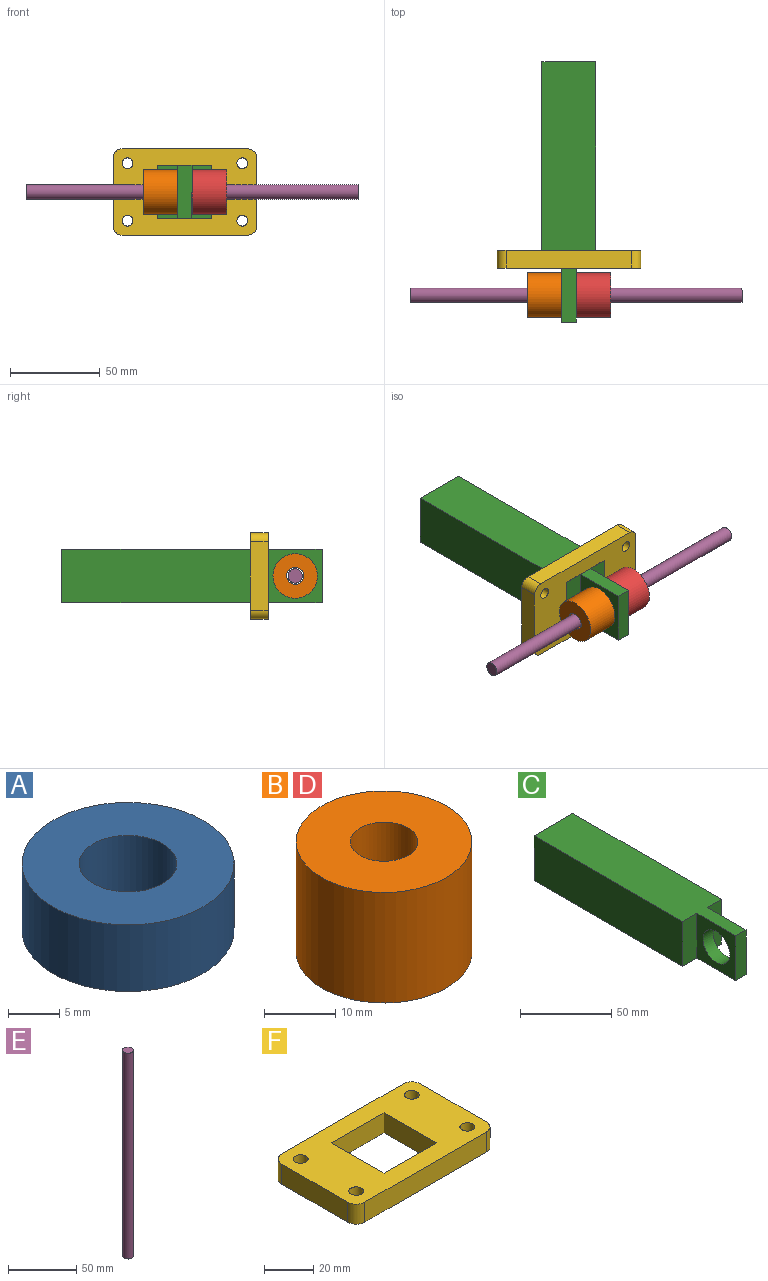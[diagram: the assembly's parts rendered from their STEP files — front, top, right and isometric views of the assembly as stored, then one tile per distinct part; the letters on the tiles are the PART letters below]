
ASSEMBLY  parts=6 mates=5
PART A: 4 faces, bbox 20.6x20.6x7.9 mm
  f0: cylinder r=4.76mm len=9.53mm, axis (0,0,-1), area 237.5mm2, adj f2,f3
  f1: cylinder r=10.32mm len=20.64mm, axis (0,0,-1), area 514.6mm2, adj f2,f3
  f2: plane 20.64x20.64mm, normal (0,0,1), area 263.3mm2, adj f0,f1
  f3: plane 20.64x20.64mm, normal (0,0,-1), area 263.3mm2, adj f0,f1
PART B: 4 faces, bbox 24.8x24.8x19.1 mm
  f0: cylinder r=4.76mm len=19.05mm, axis (0,0,-1), area 570mm2, adj f2,f3
  f1: cylinder r=12.38mm len=24.77mm, axis (0,0,-1), area 1482.1mm2, adj f2,f3
  f2: plane 24.77x24.77mm, normal (0,0,1), area 410.4mm2, adj f0,f1
  f3: plane 24.77x24.77mm, normal (0,0,-1), area 410.4mm2, adj f0,f1
PART C: 11 faces, bbox 30x145x30 mm
  f0: plane 145x30mm, normal (0,0,-1), area 3688.1mm2, adj f3,f4,f5,f6,f7,f8,f9,f10
  f1: plane 145x30mm, normal (0,0,1), area 3688.1mm2, adj f3,f4,f5,f6,f7,f8,f9,f10
  f2: cylinder r=10.32mm len=20.64mm, axis (-1,0,0), area 514.6mm2, adj f4,f5
  f3: plane 30x7.94mm, normal (0,-1,0), area 238.1mm2, adj f0,f1,f4,f5
  f4: plane 30x30mm, normal (1,0,0), area 565.5mm2, adj f0,f1,f2,f3,f6
  f5: plane 30x30mm, normal (-1,0,0), area 565.5mm2, adj f0,f1,f2,f3,f7
  f6: plane 30x11.03mm, normal (0,-1,0), area 330.9mm2, adj f0,f1,f4,f9
  f7: plane 30x11.03mm, normal (0,-1,0), area 330.9mm2, adj f0,f1,f5,f10
  f8: plane 30x30mm, normal (0,1,0), area 900mm2, adj f0,f1,f9,f10
  f9: plane 115x30mm, normal (1,0,0), area 3450mm2, adj f0,f1,f6,f8
  f10: plane 115x30mm, normal (-1,0,0), area 3450mm2, adj f0,f1,f7,f8
PART D: same geometry as B
PART E: 3 faces, bbox 8x8x185 mm
  f0: cylinder r=4mm len=185mm, axis (0,0,-1), area 4649.6mm2, adj f1,f2
  f1: plane 8x8mm, normal (0,0,1), area 50.3mm2, adj f0
  f2: plane 8x8mm, normal (0,0,-1), area 50.3mm2, adj f0
PART F: 18 faces, bbox 80x48x10 mm
  f0: plane 30x10mm, normal (0,-1,0), area 300mm2, adj f1,f7,f8,f9
  f1: plane 30x10mm, normal (-1,0,0), area 300mm2, adj f0,f2,f8,f9
  f2: plane 30x10mm, normal (0,1,0), area 300mm2, adj f1,f7,f8,f9
  f3: plane 70x10mm, normal (0,-1,0), area 700mm2, adj f8,f9,f11,f12
  f4: plane 38x10mm, normal (1,0,0), area 380mm2, adj f8,f9,f12,f13
  f5: plane 70x10mm, normal (0,1,0), area 700mm2, adj f8,f9,f10,f13
  f6: plane 38x10mm, normal (-1,0,0), area 380mm2, adj f8,f9,f10,f11
  f7: plane 30x10mm, normal (1,0,0), area 300mm2, adj f0,f2,f8,f9
  f8: plane 80x48mm, normal (0,0,1), area 2805.4mm2, adj f0,f1,f2,f3,f4,f5,f6,f7
  f9: plane 80x48mm, normal (0,0,-1), area 2805.4mm2, adj f0,f1,f2,f3,f4,f5,f6,f7
  f10: cylinder r=5mm len=10mm, axis (0,0,1), area 78.5mm2, adj f5,f6,f8,f9
  f11: cylinder r=5mm len=10mm, axis (0,0,-1), area 78.5mm2, adj f3,f6,f8,f9
  f12: cylinder r=5mm len=10mm, axis (0,0,1), area 78.5mm2, adj f3,f4,f8,f9
  f13: cylinder r=5mm len=10mm, axis (0,0,-1), area 78.5mm2, adj f4,f5,f8,f9
  f14: cylinder r=3mm len=10mm, axis (0,0,-1), area 188.5mm2, adj f8,f9
  f15: cylinder r=3mm len=10mm, axis (0,0,-1), area 188.5mm2, adj f8,f9
  f16: cylinder r=3mm len=10mm, axis (0,0,-1), area 188.5mm2, adj f8,f9
  f17: cylinder r=3mm len=10mm, axis (0,0,-1), area 188.5mm2, adj f8,f9
PLACE A rot(axis=(0,1,0),90deg) t=(-14.93,-0.25,0.12)mm
PLACE B rot(axis=(0,1,0),90deg) t=(-33.94,-0.25,0.12)mm
PLACE C rot(axis=(0,1,0),0deg) t=(-10.96,-0.25,0.12)mm fixed
PLACE D rot(axis=(0,1,0),90deg) t=(-6.8,-0.25,0.12)mm
PLACE E rot(axis=(0.71,0,-0.71),180deg) t=(-6.99,-0.25,0.12)mm
PLACE F rot(axis=(-1,0,0),90deg) t=(-10.96,14.75,0.12)mm
MATE ball A.f0 <-> E.f0  axis (1,0,0) through (-6.99,-0.25,0.12)mm
MATE fastened C.f7 <-> F.f9  axis (0,-1,0) through (-25.96,14.75,15.12)mm
MATE slider E.f0 <-> D.f0  axis (1,0,0) through (-6.99,-0.25,0.12)mm
MATE slider E.f0 <-> B.f0  axis (1,0,0) through (-6.99,-0.25,0.12)mm
MATE fastened C.f2 <-> A.f0  axis (1,0,0) through (-6.99,-0.25,0.12)mm
